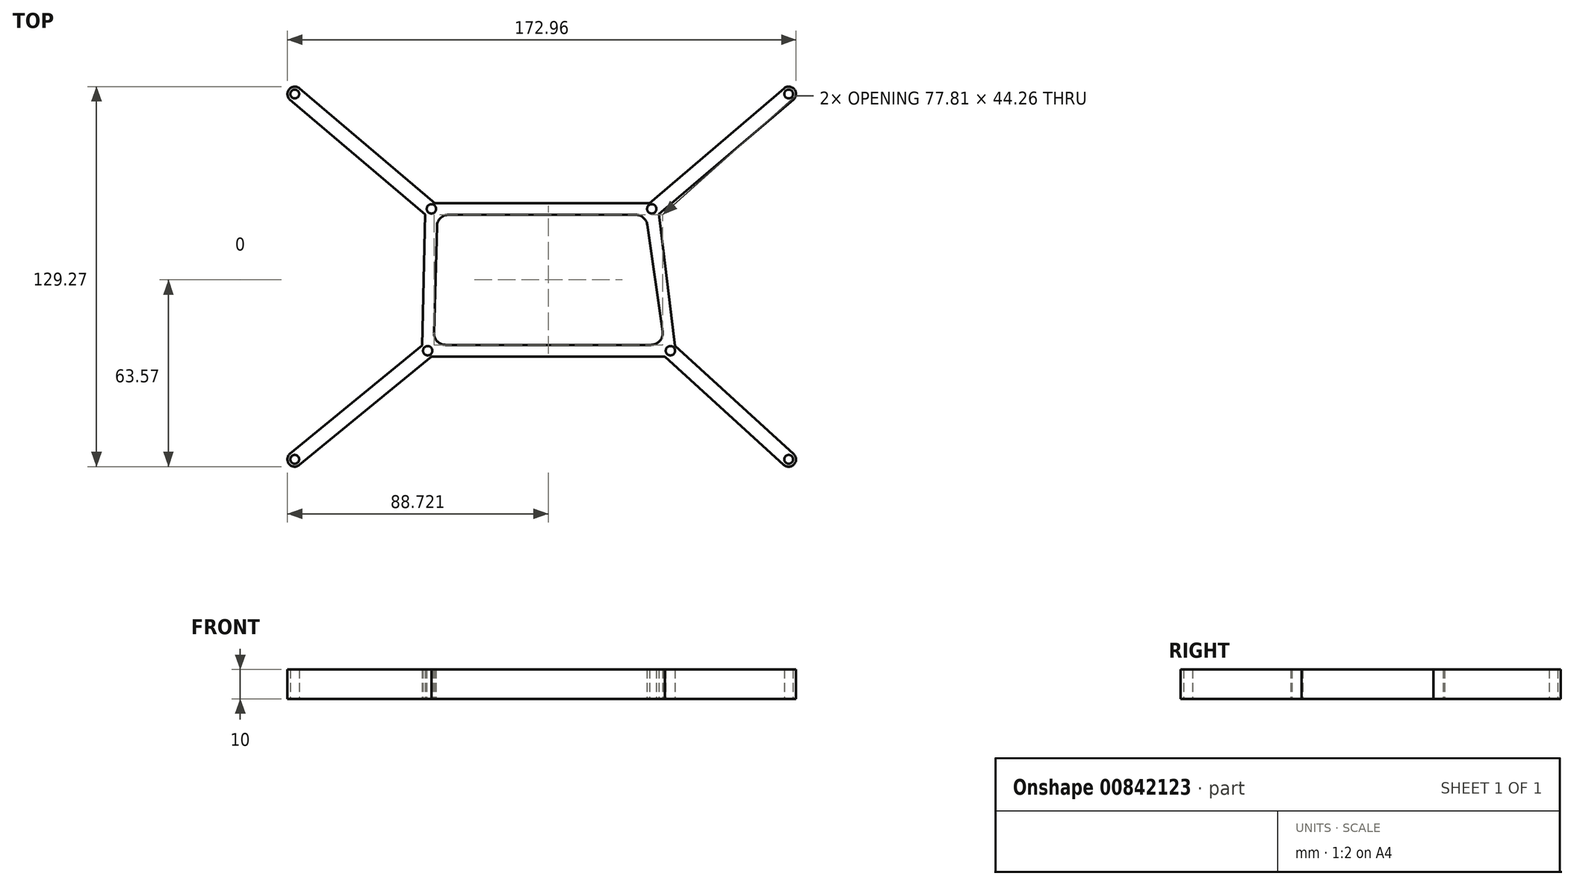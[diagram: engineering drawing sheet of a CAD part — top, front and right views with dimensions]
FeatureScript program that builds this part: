
annotation { "Feature Type Name" : "Feature", "Feature Type Description" : "" }
export const myFeature = defineFeature(function(context is Context, id is Id, definition is map)
    precondition{}
    {
        {
            var Q0;
            Q0=qCreatedBy(makeId("Top.planeOp"),FACE);
            var sketch = newSketch(context, id + "F0", { "sketchPlane" : qUnion([Q0])});
            skCircle(sketch, "E0", {"center": v(90.17, 50.8) * mm, "radius": 1.59 * mm});
            skCircle(sketch, "E1", {"center": v(13.97, 2.54) * mm, "radius": 1.59 * mm});
            skCircle(sketch, "E2", {"center": v(15.24, 50.8) * mm, "radius": 1.59 * mm});
            skCircle(sketch, "E3", {"center": v(96.52, 2.54) * mm, "radius": 1.59 * mm});
            skLineSegment(sketch, "E4", {"start": v(0, 0) * mm, "end": v(0, 53.34) * mm, "construction": true});
            skLineSegment(sketch, "E5", {"start": v(0, 53.34) * mm, "end": v(101.6, 53.34) * mm, "construction": true});
            skLineSegment(sketch, "E6", {"start": v(101.6, 53.34) * mm, "end": v(101.6, 0) * mm, "construction": true});
            skLineSegment(sketch, "E7", {"start": v(101.6, 0) * mm, "end": v(0, 0) * mm, "construction": true});
            skLineSegment(sketch, "E8", {"start": v(21.13, 48.8) * mm, "end": v(84.7, 48.8) * mm});
            skLineSegment(sketch, "E9", {"start": v(89.9, 4.54) * mm, "end": v(20.09, 4.54) * mm});
            skLineSegment(sketch, "E10", {"start": v(93.86, 9.1) * mm, "end": v(88.66, 45.37) * mm});
            skLineSegment(sketch, "E11", {"start": v(17.13, 44.91) * mm, "end": v(16.09, 8.65) * mm});
            skLineSegment(sketch, "E12", {"start": v(13.15, 48.99) * mm, "end": v(12.06, 4.4) * mm});
            skLineSegment(sketch, "E13", {"start": v(15.24, 0.54) * mm, "end": v(94.7, 0.54) * mm});
            skLineSegment(sketch, "E14", {"start": v(98.07, 4.23) * mm, "end": v(92.63, 49) * mm});
            skLineSegment(sketch, "E15", {"start": v(89.39, 52.8) * mm, "end": v(16.38, 52.8) * mm});
            skPoint(sketch, "E16.visualSharp", {"position": v(88.17, 48.8) * mm});
            skArc(sketch, "E16.filletArc", {"start": v(88.66, 45.37) * mm, "mid": v(87.32, 47.82) * mm, "end": v(84.7, 48.8) * mm});
            skPoint(sketch, "E17.visualSharp", {"position": v(94.52, 4.54) * mm});
            skArc(sketch, "E17.filletArc", {"start": v(89.9, 4.54) * mm, "mid": v(92.93, 5.92) * mm, "end": v(93.86, 9.1) * mm});
            skPoint(sketch, "E18.visualSharp", {"position": v(15.97, 4.54) * mm});
            skArc(sketch, "E18.filletArc", {"start": v(16.09, 8.65) * mm, "mid": v(17.22, 5.75) * mm, "end": v(20.09, 4.54) * mm});
            skPoint(sketch, "E19.visualSharp", {"position": v(17.24, 48.8) * mm});
            skArc(sketch, "E19.filletArc", {"start": v(21.13, 48.8) * mm, "mid": v(18.34, 47.67) * mm, "end": v(17.13, 44.91) * mm});
            skLineSegment(sketch, "E20", {"start": v(89.39, 52.8) * mm, "end": v(135.1, 91.78) * mm});
            skLineSegment(sketch, "E21", {"start": v(92.63, 49) * mm, "end": v(138.35, 87.97) * mm});
            skArc(sketch, "E22", {"start": v(138.35, 87.97) * mm, "mid": v(138.63, 91.5) * mm, "end": v(135.1, 91.78) * mm});
            skLineSegment(sketch, "E23", {"start": v(98.07, 4.23) * mm, "end": v(138.42, -32.55) * mm});
            skLineSegment(sketch, "E24", {"start": v(94.7, 0.54) * mm, "end": v(135.05, -36.24) * mm});
            skArc(sketch, "E25", {"start": v(135.05, -36.24) * mm, "mid": v(138.58, -36.08) * mm, "end": v(138.42, -32.55) * mm});
            skLineSegment(sketch, "E26", {"start": v(12.06, 4.4) * mm, "end": v(-32.82, -32.46) * mm});
            skLineSegment(sketch, "E27", {"start": v(15.24, 0.54) * mm, "end": v(-29.65, -36.33) * mm});
            skArc(sketch, "E28", {"start": v(-32.82, -32.46) * mm, "mid": v(-33.16, -35.98) * mm, "end": v(-29.65, -36.33) * mm});
            skLineSegment(sketch, "E29", {"start": v(13.15, 48.99) * mm, "end": v(-32.85, 87.97) * mm});
            skLineSegment(sketch, "E30", {"start": v(16.38, 52.8) * mm, "end": v(-29.62, 91.78) * mm});
            skArc(sketch, "E31", {"start": v(-29.62, 91.78) * mm, "mid": v(-33.14, 91.5) * mm, "end": v(-32.85, 87.97) * mm});
            skLineSegment(sketch, "E32.bottom", {"start": v(-31.23, 89.87) * mm, "end": v(136.73, 89.87) * mm, "construction": true});
            skLineSegment(sketch, "E32.top", {"start": v(-31.23, -34.4) * mm, "end": v(136.73, -34.4) * mm, "construction": true});
            skLineSegment(sketch, "E32.left", {"start": v(-31.23, 89.87) * mm, "end": v(-31.23, -34.4) * mm, "construction": true});
            skLineSegment(sketch, "E32.right", {"start": v(136.73, 89.87) * mm, "end": v(136.73, -34.4) * mm, "construction": true});
            skPoint(sketch, "E33.orphan", {"position": v(92.17, 52.8) * mm});
            skPoint(sketch, "E34.orphan", {"position": v(98.52, 0.54) * mm});
            skPoint(sketch, "E35.orphan", {"position": v(11.97, 0.54) * mm});
            skPoint(sketch, "E36.orphan", {"position": v(13.24, 52.8) * mm});
            skCircle(sketch, "E37", {"center": v(-31.23, 89.87) * mm, "radius": 1.5 * mm});
            skCircle(sketch, "E38", {"center": v(136.73, 89.87) * mm, "radius": 1.5 * mm});
            skCircle(sketch, "E39", {"center": v(136.73, -34.4) * mm, "radius": 1.5 * mm});
            skCircle(sketch, "E40", {"center": v(-31.23, -34.4) * mm, "radius": 1.5 * mm});
            skSolve(sketch);
        }
        {
            var Q0;
            Q0=makeQuery(id+"F0.imprint","IMPRINT",FACE,{"disambiguationData":[TD([[makeQuery(id+"F0.imprint","IMPRINT",EDGE,{"derivedFrom":sQuery(id+"F0.wireOp",EDGE,"E0")}),-1.0]])]});
            extrude(context, id + "F1", {"entities" : qUnion([Q0]), "depth" : 10 * mm, "offsetDistance" : 25 * mm});
        }
    });
